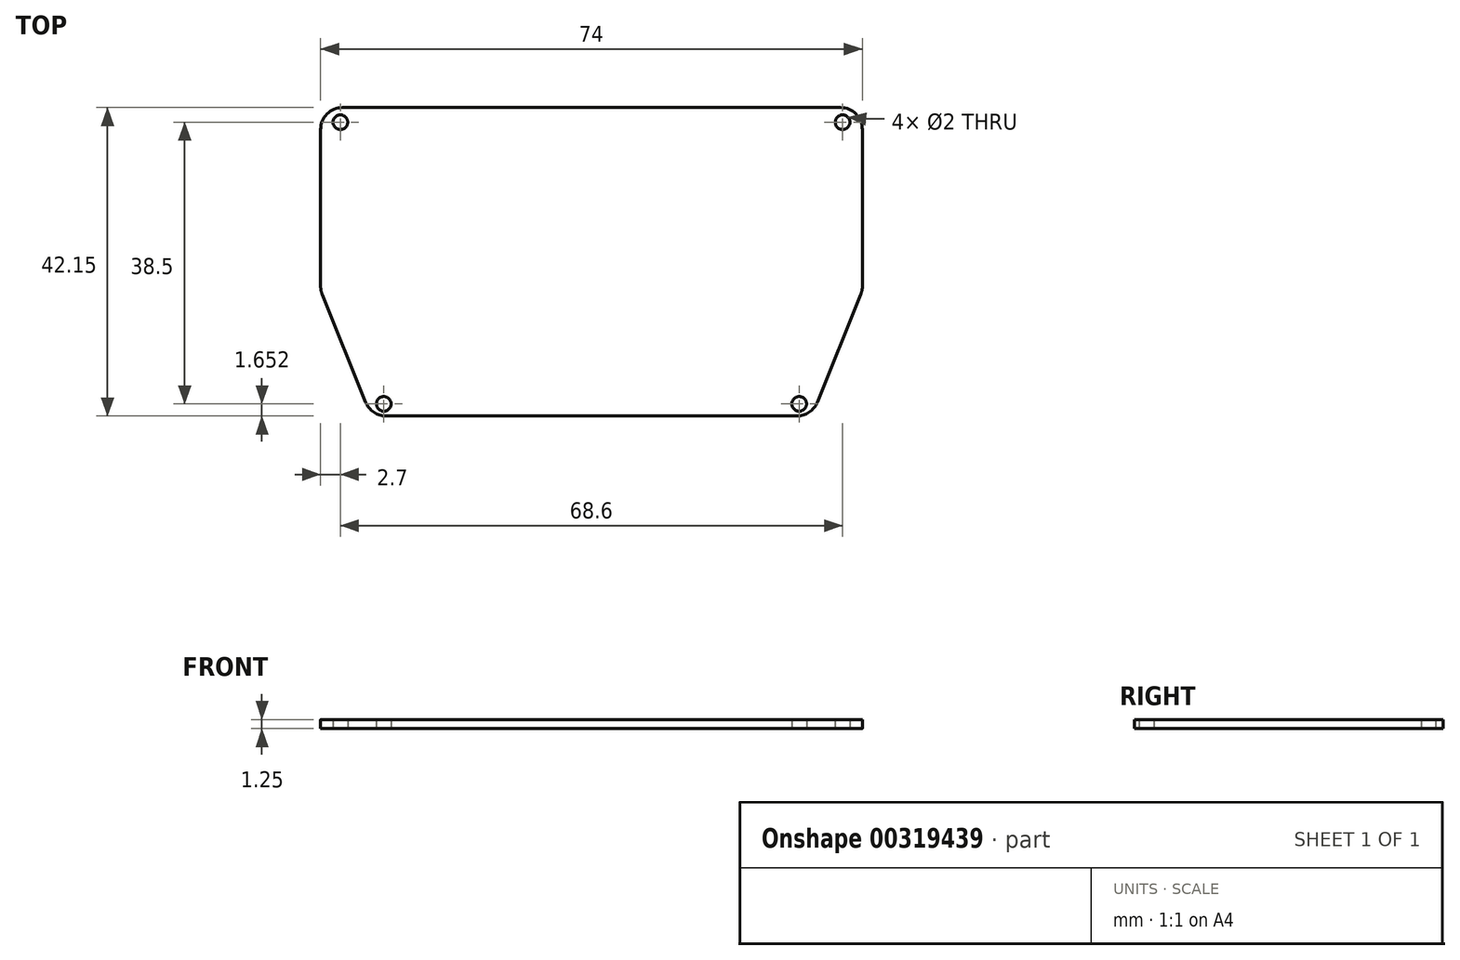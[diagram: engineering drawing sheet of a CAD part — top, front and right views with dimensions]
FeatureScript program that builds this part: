
annotation { "Feature Type Name" : "Feature", "Feature Type Description" : "" }
export const myFeature = defineFeature(function(context is Context, id is Id, definition is map)
    precondition{}
    {
        {
            var Q0;
            Q0=qCreatedBy(makeId("Top.planeOp"),FACE);
            var sketch = newSketch(context, id + "F0", { "sketchPlane" : qUnion([Q0])});
            skLineSegment(sketch, "E0.bottom", {"start": v(-7, 0) * mm, "end": v(-67, 0) * mm});
            skLineSegment(sketch, "E0.top", {"start": v(0, 42.35) * mm, "end": v(-74, 42.35) * mm});
            skLineSegment(sketch, "E0.left", {"start": v(0, 17.35) * mm, "end": v(0, 42.35) * mm});
            skLineSegment(sketch, "E0.right", {"start": v(-74, 17.35) * mm, "end": v(-74, 42.35) * mm});
            skLineSegment(sketch, "E1", {"start": v(0, 17.35) * mm, "end": v(-6.92, 0.2) * mm});
            skLineSegment(sketch, "E2", {"start": v(-67.08, 0.2) * mm, "end": v(-74, 17.35) * mm});
            skPoint(sketch, "E3.orphan", {"position": v(-74, 0) * mm});
            skPoint(sketch, "E4.orphan", {"position": v(0, 0) * mm});
            skCircle(sketch, "E5", {"center": v(-65.38, 1.85) * mm, "radius": 1 * mm});
            skCircle(sketch, "E6", {"center": v(-8.62, 1.85) * mm, "radius": 1 * mm});
            skCircle(sketch, "E7", {"center": v(-71.3, 40.35) * mm, "radius": 1 * mm});
            skCircle(sketch, "E8", {"center": v(-2.7, 40.35) * mm, "radius": 1 * mm});
            skLineSegment(sketch, "E9", {"start": v(-67.08, 0.2) * mm, "end": v(-6.92, 0.2) * mm});
            skSolve(sketch);
        }
        {
            var Q0;
            Q0=makeQuery(id+"F0.imprint","IMPRINT",FACE,{"disambiguationData":[TD([[makeQuery(id+"F0.imprint","IMPRINT",EDGE,{"derivedFrom":sQuery(id+"F0.wireOp",EDGE,"E0.top")}),1.0]])]});
            extrude(context, id + "F1", {"entities" : qUnion([Q0]), "depth" : 1.25 * mm});
        }
        {
            var Q0;
            Q0=makeQuery(id+"F1.opExtrude","SWEPT_EDGE",EDGE,{"disambiguationData":[OSD([sQuery(id+"F0.wireOp",EDGE,"cLTiyaKl-XE7g-fnmk-SjMA-JzOKtulOQLZJ"),sQuery(id+"F0.wireOp",EDGE,"E2")])]});
            var Q1;
            Q1=makeQuery(id+"F1.opExtrude","SWEPT_EDGE",EDGE,{"disambiguationData":[OSD([sQuery(id+"F0.wireOp",EDGE,"E1"),sQuery(id+"F0.wireOp",EDGE,"cLTiyaKl-XE7g-fnmk-SjMA-JzOKtulOQLZJ")])]});
            var Q2;
            Q2=makeQuery(id+"F1.opExtrude","SWEPT_EDGE",EDGE,{"disambiguationData":[OSD([sQuery(id+"F0.wireOp",EDGE,"E0.top"),sQuery(id+"F0.wireOp",EDGE,"E0.left")])]});
            var Q3;
            Q3=makeQuery(id+"F1.opExtrude","SWEPT_EDGE",EDGE,{"disambiguationData":[OSD([sQuery(id+"F0.wireOp",EDGE,"E0.top"),sQuery(id+"F0.wireOp",EDGE,"E0.right")])]});
            var Q4;
            Q4=makeQuery(id+"F1.opExtrude","SWEPT_EDGE",EDGE,{"disambiguationData":[OSD([sQuery(id+"F0.wireOp",EDGE,"E0.right"),sQuery(id+"F0.wireOp",EDGE,"E2")])]});
            var Q5;
            Q5=makeQuery(id+"F1.opExtrude","SWEPT_EDGE",EDGE,{"disambiguationData":[OSD([sQuery(id+"F0.wireOp",EDGE,"E0.left"),sQuery(id+"F0.wireOp",EDGE,"E1")])]});
            fillet(context, id + "F2", {"entities" : qUnion([Q0, Q1, Q2, Q3, Q4, Q5]), "radius" : 3 * mm, "tangentPropagation" : true, "allowEdgeOverflow" : false});
        }
    });
